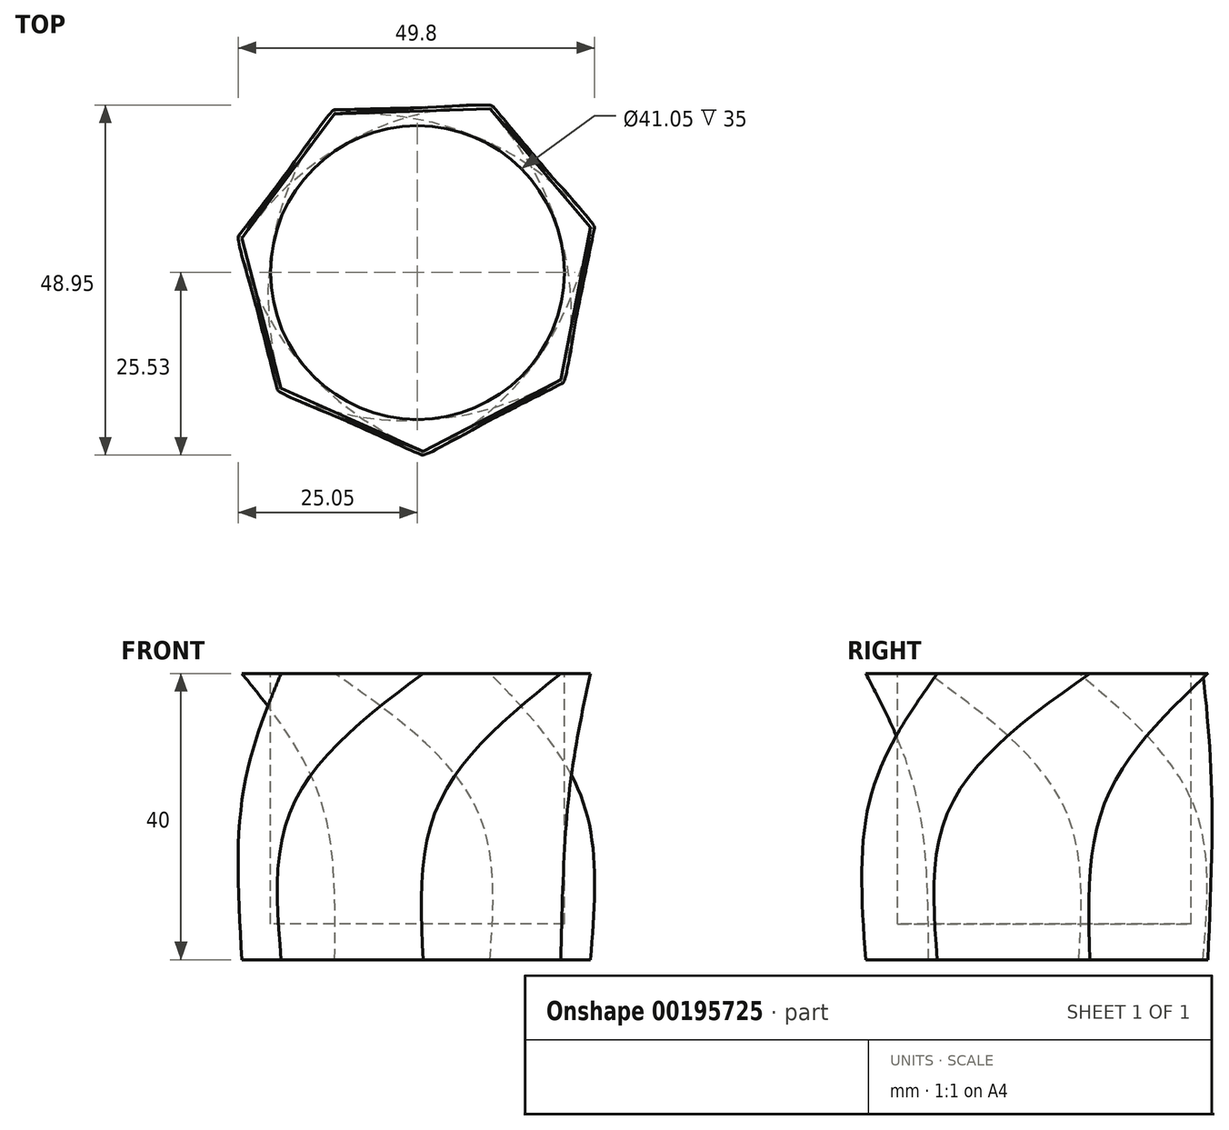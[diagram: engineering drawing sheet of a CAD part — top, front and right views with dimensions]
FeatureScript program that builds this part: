
annotation { "Feature Type Name" : "Feature", "Feature Type Description" : "" }
export const myFeature = defineFeature(function(context is Context, id is Id, definition is map)
    precondition{}
    {
        {
            var Q0;
            Q0=qCreatedBy(makeId("Top.planeOp"),FACE);
            var sketch = newSketch(context, id + "F0", { "sketchPlane" : qUnion([Q0])});
            skCircle(sketch, "E0.cCircle", {"center": v(0, 0) * mm, "radius": 25 * mm, "construction": true});
            skLineSegment(sketch, "E0.0", {"start": v(20.02, -14.97) * mm, "end": v(0.78, -24.99) * mm});
            skLineSegment(sketch, "E0.1", {"start": v(0.78, -24.99) * mm, "end": v(-19.05, -16.2) * mm});
            skLineSegment(sketch, "E0.2", {"start": v(-19.05, -16.2) * mm, "end": v(-24.54, 4.8) * mm});
            skLineSegment(sketch, "E0.3", {"start": v(-24.54, 4.8) * mm, "end": v(-11.55, 22.17) * mm});
            skLineSegment(sketch, "E0.4", {"start": v(-11.55, 22.17) * mm, "end": v(10.14, 22.85) * mm});
            skLineSegment(sketch, "E0.5", {"start": v(10.14, 22.85) * mm, "end": v(24.19, 6.32) * mm});
            skLineSegment(sketch, "E0.6", {"start": v(24.19, 6.32) * mm, "end": v(20.02, -14.97) * mm});
            skSolve(sketch);
        }
        {
            var Q0;
            Q0=qCreatedBy(makeId("Top.planeOp"),FACE);
            cPlane(context, id + "F1", {"entities" : qUnion([Q0]), "cplaneType" : CPlaneType.OFFSET, "offset" : 20 * mm, "width" : 150 * mm, "height" : 150 * mm});
        }
        {
            var Q0;
            Q0=qCreatedBy(id+"F1.planeOp",FACE);
            var sketch = newSketch(context, id + "F2", { "sketchPlane" : qUnion([Q0])});
            skCircle(sketch, "E1.cCircle", {"center": v(0, 0) * mm, "radius": 25 * mm, "construction": true});
            skLineSegment(sketch, "E1.0", {"start": v(2.27, -24.9) * mm, "end": v(-18.05, -17.3) * mm});
            skLineSegment(sketch, "E1.1", {"start": v(-18.05, -17.3) * mm, "end": v(-24.78, 3.33) * mm});
            skLineSegment(sketch, "E1.2", {"start": v(-24.78, 3.33) * mm, "end": v(-12.85, 21.45) * mm});
            skLineSegment(sketch, "E1.3", {"start": v(-12.85, 21.45) * mm, "end": v(8.76, 23.42) * mm});
            skLineSegment(sketch, "E1.4", {"start": v(8.76, 23.42) * mm, "end": v(23.77, 7.75) * mm});
            skLineSegment(sketch, "E1.5", {"start": v(23.77, 7.75) * mm, "end": v(20.88, -13.75) * mm});
            skLineSegment(sketch, "E1.6", {"start": v(20.88, -13.75) * mm, "end": v(2.27, -24.9) * mm});
            skSolve(sketch);
        }
        {
            var Q0;
            Q0=qCreatedBy(id+"F1.planeOp",FACE);
            cPlane(context, id + "F3", {"entities" : qUnion([Q0]), "cplaneType" : CPlaneType.OFFSET, "offset" : 20 * mm, "width" : 150 * mm, "height" : 150 * mm});
        }
        {
            var Q0;
            Q0=qCreatedBy(id+"F3.planeOp",FACE);
            var sketch = newSketch(context, id + "F4", { "sketchPlane" : qUnion([Q0])});
            skCircle(sketch, "E2.cCircle", {"center": v(0, 0) * mm, "radius": 25 * mm, "construction": true});
            skLineSegment(sketch, "E2.0", {"start": v(20.02, -14.97) * mm, "end": v(0.78, -24.99) * mm});
            skLineSegment(sketch, "E2.1", {"start": v(0.78, -24.99) * mm, "end": v(-19.05, -16.2) * mm});
            skLineSegment(sketch, "E2.2", {"start": v(-19.05, -16.2) * mm, "end": v(-24.54, 4.8) * mm});
            skLineSegment(sketch, "E2.3", {"start": v(-24.54, 4.8) * mm, "end": v(-11.55, 22.17) * mm});
            skLineSegment(sketch, "E2.4", {"start": v(-11.55, 22.17) * mm, "end": v(10.14, 22.85) * mm});
            skLineSegment(sketch, "E2.5", {"start": v(10.14, 22.85) * mm, "end": v(24.19, 6.32) * mm});
            skLineSegment(sketch, "E2.6", {"start": v(24.19, 6.32) * mm, "end": v(20.02, -14.97) * mm});
            skSolve(sketch);
        }
        {
            var Q0;
            Q0=makeQuery(id+"F0.imprint","IMPRINT",FACE,{"disambiguationData":[TD([[makeQuery(id+"F0.imprint","IMPRINT",EDGE,{"derivedFrom":sQuery(id+"F0.wireOp",EDGE,"E0.0")}),-1.0]])]});
            var Q1;
            Q1=makeQuery(id+"F2.imprint","IMPRINT",FACE,{"disambiguationData":[TD([[makeQuery(id+"F2.imprint","IMPRINT",EDGE,{"derivedFrom":sQuery(id+"F2.wireOp",EDGE,"E1.0")}),-1.0]])]});
            var Q2;
            Q2=makeQuery(id+"F4.imprint","IMPRINT",FACE,{"disambiguationData":[TD([[makeQuery(id+"F4.imprint","IMPRINT",EDGE,{"derivedFrom":sQuery(id+"F4.wireOp",EDGE,"E2.0")}),-1.0]])]});
            var Q3;
            Q3=sQuery(id+"F0.wireOp",VERTEX,"E0.6.end");
            var Q4;
            Q4=sQuery(id+"F2.wireOp",VERTEX,"E1.6.start");
            var Q5;
            Q5=sQuery(id+"F4.wireOp",VERTEX,"E2.6.start");
            loft(context, id + "F5", {"sheetProfilesArray" : [{ "sheetProfileEntities" : qUnion([Q0]) }, { "sheetProfileEntities" : qUnion([Q1]) }, { "sheetProfileEntities" : qUnion([Q2]) }], "matchConnections" : true, "connections" : [{ "connectionEntities" : qUnion([Q3, Q4, Q5]), "connectionEdgeQueries" : qUnion([]), "connectionEdgeParameters" : [] }]});
        }
        {
            var Q0;
            Q0=qCreatedBy(id+"F3.planeOp",FACE);
            var sketch = newSketch(context, id + "F6", { "sketchPlane" : qUnion([Q0])});
            skCircle(sketch, "E3", {"center": v(0, 0) * mm, "radius": 20.52 * mm});
            skSolve(sketch);
        }
        {
            var Q0;
            Q0=makeQuery(id+"F6.imprint","IMPRINT",FACE,{"disambiguationData":[TD([[makeQuery(id+"F6.imprint","IMPRINT",EDGE,{"derivedFrom":sQuery(id+"F6.wireOp",EDGE,"E3")}),1.0]])]});
            extrude(context, id + "F7", {"entities" : qUnion([Q0]), "operationType" : NewBodyOperationType.REMOVE, "oppositeDirection" : true, "depth" : 35 * mm});
        }
    });
